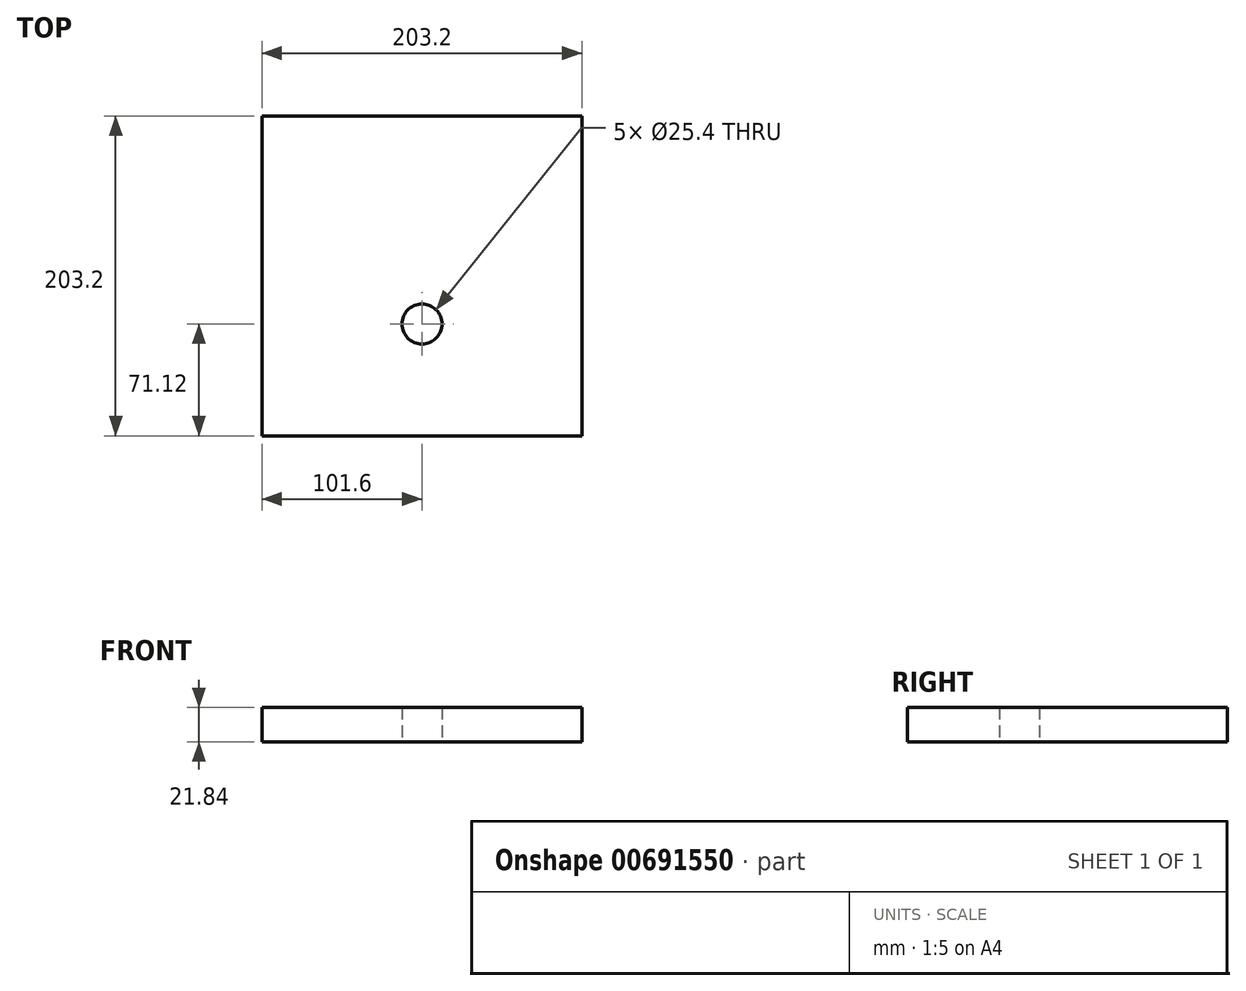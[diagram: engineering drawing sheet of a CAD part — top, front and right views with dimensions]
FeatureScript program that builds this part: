
annotation { "Feature Type Name" : "Feature", "Feature Type Description" : "" }
export const myFeature = defineFeature(function(context is Context, id is Id, definition is map)
    precondition{}
    {
        {
            var Q0;
            Q0=qCreatedBy(makeId("Top.planeOp"),FACE);
            var sketch = newSketch(context, id + "F0", { "sketchPlane" : qUnion([Q0])});
            skLineSegment(sketch, "E0.bottom", {"start": v(101.6, -101.6) * mm, "end": v(-101.6, -101.6) * mm});
            skLineSegment(sketch, "E0.top", {"start": v(101.6, 101.6) * mm, "end": v(-101.6, 101.6) * mm});
            skLineSegment(sketch, "E0.left", {"start": v(101.6, -101.6) * mm, "end": v(101.6, 101.6) * mm});
            skLineSegment(sketch, "E0.right", {"start": v(-101.6, -101.6) * mm, "end": v(-101.6, 101.6) * mm});
            skPoint(sketch, "E0.middle", {"position": v(0, 0) * mm});
            skLineSegment(sketch, "E1", {"start": v(0, -101.6) * mm, "end": v(0, -30.48) * mm});
            skCircle(sketch, "E2", {"center": v(0, -30.48) * mm, "radius": 12.7 * mm});
            skSolve(sketch);
        }
        {
            var Q0;
            Q0 = qSketchRegion(id + "F0", true);
            extrude(context, id + "F1", {"entities" : qUnion([Q0]), "depth" : 21.84 * mm, "offsetDistance" : 25.4 * mm});
        }
    });
